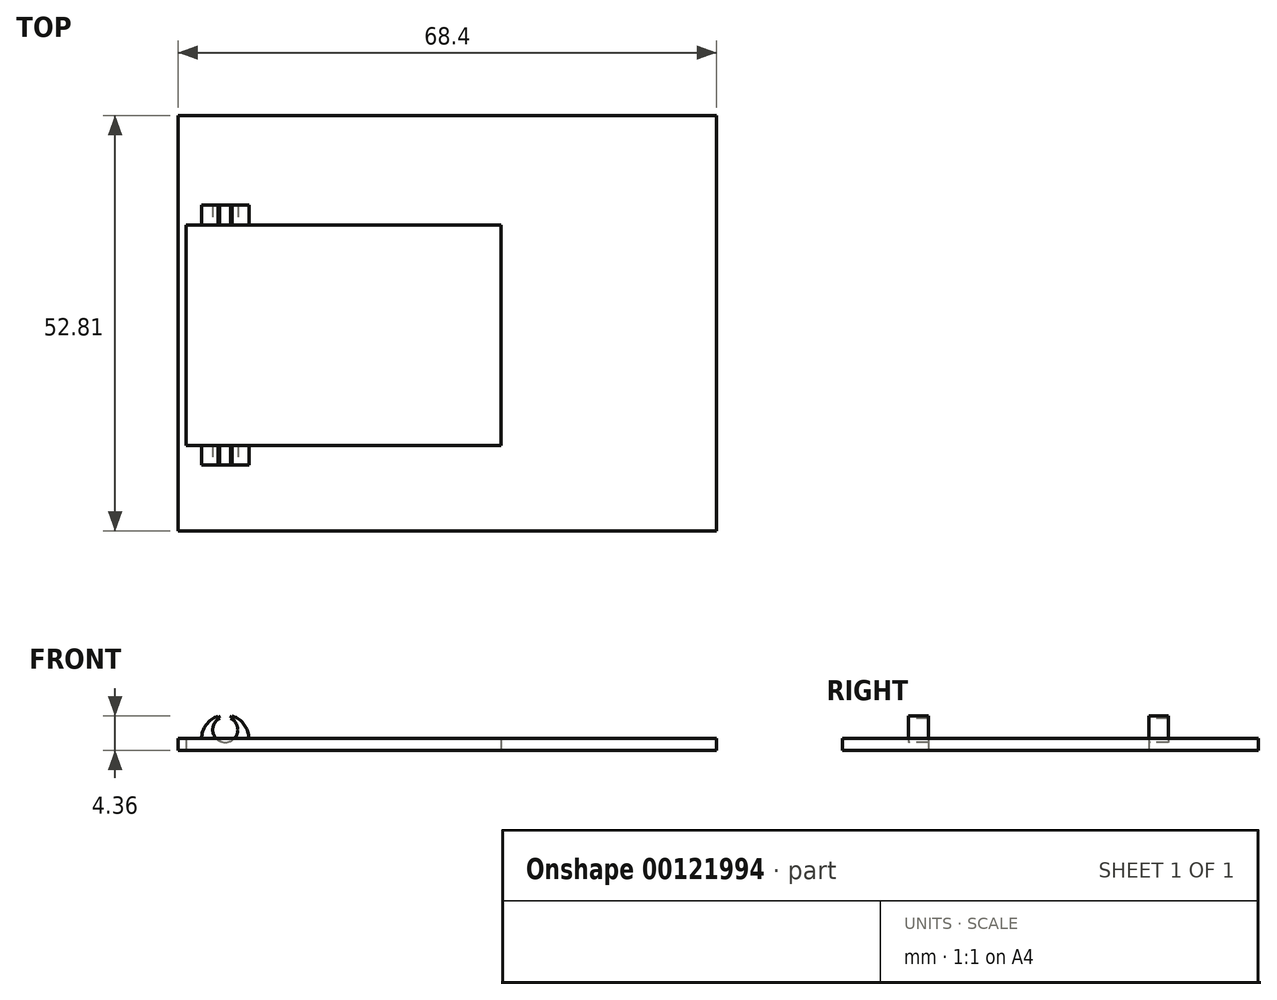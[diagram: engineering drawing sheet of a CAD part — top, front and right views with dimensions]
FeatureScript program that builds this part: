
annotation { "Feature Type Name" : "Feature", "Feature Type Description" : "" }
export const myFeature = defineFeature(function(context is Context, id is Id, definition is map)
    precondition{}
    {
        {
            var Q0;
            Q0=qCreatedBy(makeId("Front.planeOp"),FACE);
            var sketch = newSketch(context, id + "F0", { "sketchPlane" : qUnion([Q0])});
            skLineSegment(sketch, "E0.bottom", {"start": v(36.5, -11) * mm, "end": v(-36.5, -11) * mm});
            skLineSegment(sketch, "E0.top", {"start": v(36.5, 11) * mm, "end": v(-36.5, 11) * mm});
            skLineSegment(sketch, "E0.left", {"start": v(36.5, -11) * mm, "end": v(36.5, 11) * mm});
            skLineSegment(sketch, "E0.right", {"start": v(-36.5, -11) * mm, "end": v(-36.5, 11) * mm});
            skPoint(sketch, "E0.middle", {"position": v(0, 0) * mm});
            skFitSpline(sketch, "E1", {"points": [v(-0.93, -0.38) * mm, v(-0.75, 0.37) * mm], "startDerivative": vector(0.3, 0.98) * mm, "endDerivative": vector(-0.8, 0.77) * mm});
            skFitSpline(sketch, "E2", {"points": [v(0.91, -0.38) * mm, v(0.8, 0.37) * mm], "startDerivative": vector(-0.3, 0.98) * mm, "endDerivative": vector(1, 0.77) * mm});
            skSolve(sketch);
        }
        {
            var Q0;
            Q0=makeQuery(id+"F0.imprint","IMPRINT",FACE,{"disambiguationData":[TD([[makeQuery(id+"F0.imprint","IMPRINT",EDGE,{"derivedFrom":sQuery(id+"F0.wireOp",EDGE,"E0.bottom")}),-1.0]])]});
            extrude(context, id + "F1", {"entities" : qUnion([Q0]), "depth" : 58 * mm, "symmetric" : true});
        }
        {
            var Q0;
            Q0=makeQuery(id+"F1.opExtrude","SWEPT_FACE",FACE,{"disambiguationData":[OSD([sQuery(id+"F0.wireOp",EDGE,"E0.top")])]});
            var sketch = newSketch(context, id + "F2", { "sketchPlane" : qUnion([Q0])});
            skLineSegment(sketch, "E3.bottom", {"start": v(-34.5, 27) * mm, "end": v(34.5, 27) * mm});
            skLineSegment(sketch, "E3.top", {"start": v(-34.5, -27) * mm, "end": v(34.5, -27) * mm});
            skLineSegment(sketch, "E3.left", {"start": v(-34.5, 27) * mm, "end": v(-34.5, -27) * mm});
            skLineSegment(sketch, "E3.right", {"start": v(34.5, 27) * mm, "end": v(34.5, -27) * mm});
            skPoint(sketch, "E3.middle", {"position": v(0, 0) * mm});
            skSolve(sketch);
        }
        {
            var Q0;
            Q0=qSketchRegion(id+"F2",true);
            extrude(context, id + "F3", {"entities" : qUnion([Q0]), "operationType" : NewBodyOperationType.REMOVE, "oppositeDirection" : true, "depth" : 19 * mm});
        }
        {
            var Q0;
            Q0=makeQuery(id+"F1.opExtrude","SWEPT_FACE",FACE,{"disambiguationData":[OSD([sQuery(id+"F0.wireOp",EDGE,"E0.bottom")])]});
            var sketch = newSketch(context, id + "F4", { "sketchPlane" : qUnion([Q0])});
            skLineSegment(sketch, "E4.bottom", {"start": v(-33.5, 15) * mm, "end": v(8.5, 15) * mm});
            skLineSegment(sketch, "E4.top", {"start": v(-33.5, -13) * mm, "end": v(8.5, -13) * mm});
            skLineSegment(sketch, "E4.left", {"start": v(-33.5, 15) * mm, "end": v(-33.5, -13) * mm});
            skLineSegment(sketch, "E4.right", {"start": v(8.5, 15) * mm, "end": v(8.5, -13) * mm});
            skSolve(sketch);
        }
        {
            var Q0;
            Q0=qSketchRegion(id+"F4",true);
            extrude(context, id + "F5", {"entities" : qUnion([Q0]), "operationType" : NewBodyOperationType.REMOVE, "endBound" : BoundingType.THROUGH_ALL, "oppositeDirection" : true, "depth" : 25 * mm});
        }
        {
            var Q0;
            Q0=makeQuery(id+"F5.boolean.opBoolean","COPY",FACE,{"derivedFrom":makeQuery(id+"F5.opExtrude","SWEPT_FACE",FACE,{"disambiguationData":[OSD([sQuery(id+"F4.wireOp",EDGE,"E4.right")])]})});
            var sketch = newSketch(context, id + "F6", { "sketchPlane" : qUnion([Q0])});
            skLineSegment(sketch, "E5.bottom", {"start": v(-13, -8) * mm, "end": v(15, -8) * mm});
            skLineSegment(sketch, "E5.top", {"start": v(-13, -9.5) * mm, "end": v(15, -9.5) * mm});
            skLineSegment(sketch, "E5.left", {"start": v(-13, -8) * mm, "end": v(-13, -9.5) * mm});
            skLineSegment(sketch, "E5.right", {"start": v(15, -8) * mm, "end": v(15, -9.5) * mm});
            skSolve(sketch);
        }
        {
            var Q0;
            Q0=qSketchRegion(id+"F6",true);
            extrude(context, id + "F7", {"entities" : qUnion([Q0]), "operationType" : NewBodyOperationType.ADD, "depth" : 2 * mm});
        }
        {
            var Q0;
            Q0=makeQuery(id+"F1.opExtrude","CAP_FACE",FACE,{"disambiguationData":[OSD([sQuery(id+"F0.wireOp",EDGE,"E0.bottom"),sQuery(id+"F0.wireOp",EDGE,"E0.top"),sQuery(id+"F0.wireOp",EDGE,"E0.left"),sQuery(id+"F0.wireOp",EDGE,"E0.right")])],"isStart":false});
            var sketch = newSketch(context, id + "F8", { "sketchPlane" : qUnion([Q0])});
            skLineSegment(sketch, "E6.bottom", {"start": v(-36.5, 11) * mm, "end": v(36.5, 11) * mm});
            skLineSegment(sketch, "E6.top", {"start": v(-36.5, -2.74) * mm, "end": v(36.5, -2.74) * mm});
            skLineSegment(sketch, "E6.left", {"start": v(-36.5, 11) * mm, "end": v(-36.5, -2.74) * mm});
            skLineSegment(sketch, "E6.right", {"start": v(36.5, 11) * mm, "end": v(36.5, -2.74) * mm});
            skSolve(sketch);
        }
        {
            var Q0;
            Q0 = qSketchRegion(id + "F8", true);
            extrude(context, id + "F9", {"entities" : qUnion([Q0]), "operationType" : NewBodyOperationType.REMOVE, "endBound" : BoundingType.THROUGH_ALL, "oppositeDirection" : true, "depth" : 25 * mm});
        }
        {
            var Q0;
            Q0=makeQuery(id+"F7.boolean.opBoolean","MERGE",FACE,{"derivedFrom":[makeQuery(id+"F3.boolean.opBoolean","COPY",FACE,{"derivedFrom":makeQuery(id+"F3.opExtrude","CAP_FACE",FACE,{"disambiguationData":[OSD([sQuery(id+"F2.wireOp",EDGE,"E3.bottom"),sQuery(id+"F2.wireOp",EDGE,"E3.top"),sQuery(id+"F2.wireOp",EDGE,"E3.left"),sQuery(id+"F2.wireOp",EDGE,"E3.right")])],"isStart":false})}),makeQuery(id+"F7.opExtrude","SWEPT_FACE",FACE,{"disambiguationData":[OSD([sQuery(id+"F6.wireOp",EDGE,"E5.bottom")])]})]});
            var sketch = newSketch(context, id + "F10", { "sketchPlane" : qUnion([Q0])});
            skLineSegment(sketch, "E7.bottom", {"start": v(-31.5, 15.5) * mm, "end": v(-28.5, 15.5) * mm});
            skLineSegment(sketch, "E7.top", {"start": v(-31.5, 13) * mm, "end": v(-28.5, 13) * mm});
            skLineSegment(sketch, "E7.left", {"start": v(-31.5, 15.5) * mm, "end": v(-31.5, 13) * mm});
            skLineSegment(sketch, "E7.right", {"start": v(-28.5, 15.5) * mm, "end": v(-28.5, 13) * mm});
            skSolve(sketch);
        }
        {
            var Q0;
            Q0=makeQuery(id+"F10.imprint","IMPRINT",FACE,{"disambiguationData":[TD([[makeQuery(id+"F10.imprint","IMPRINT",EDGE,{"derivedFrom":sQuery(id+"F10.wireOp",EDGE,"E7.bottom")}),-1.0]])]});
            var Q1;
            Q1=sQuery(id+"F10.wireOp",EDGE,"E7.right");
            revolve(context, id + "F11", {"operationType" : NewBodyOperationType.ADD, "entities" : qUnion([Q0]), "axis" : qUnion([Q1]), "revolveType" : RevolveType.ONE_DIRECTION, "oppositeDirection" : true, "angle" : 180 * degree});
        }
        {
            var Q0;
            Q0=makeQuery(id+"F7.boolean.opBoolean","MERGE",FACE,{"derivedFrom":[makeQuery(id+"F3.boolean.opBoolean","COPY",FACE,{"derivedFrom":makeQuery(id+"F3.opExtrude","CAP_FACE",FACE,{"disambiguationData":[OSD([sQuery(id+"F2.wireOp",EDGE,"E3.bottom"),sQuery(id+"F2.wireOp",EDGE,"E3.top"),sQuery(id+"F2.wireOp",EDGE,"E3.left"),sQuery(id+"F2.wireOp",EDGE,"E3.right")])],"isStart":false})}),makeQuery(id+"F7.opExtrude","SWEPT_FACE",FACE,{"disambiguationData":[OSD([sQuery(id+"F6.wireOp",EDGE,"E5.bottom")])]})]});
            var sketch = newSketch(context, id + "F12", { "sketchPlane" : qUnion([Q0])});
            skLineSegment(sketch, "E8.bottom", {"start": v(-31.5, -15) * mm, "end": v(-28.5, -15) * mm});
            skLineSegment(sketch, "E8.top", {"start": v(-31.5, -17.5) * mm, "end": v(-28.5, -17.5) * mm});
            skLineSegment(sketch, "E8.left", {"start": v(-31.5, -15) * mm, "end": v(-31.5, -17.5) * mm});
            skLineSegment(sketch, "E8.right", {"start": v(-28.5, -15) * mm, "end": v(-28.5, -17.5) * mm});
            skSolve(sketch);
        }
        {
            var Q0;
            Q0=makeQuery(id+"F12.imprint","IMPRINT",FACE,{"disambiguationData":[TD([[makeQuery(id+"F12.imprint","IMPRINT",EDGE,{"derivedFrom":sQuery(id+"F12.wireOp",EDGE,"E8.bottom")}),1.0]])]});
            var Q1;
            Q1=sQuery(id+"F12.wireOp",EDGE,"E8.right");
            revolve(context, id + "F13", {"operationType" : NewBodyOperationType.ADD, "entities" : qUnion([Q0]), "axis" : qUnion([Q1]), "revolveType" : RevolveType.ONE_DIRECTION, "oppositeDirection" : true, "angle" : 180 * degree});
        }
        {
            var Q0;
            Q0=makeQuery(id+"F13.opRevolve","SWEPT_FACE",FACE,{"disambiguationData":[OSD([sQuery(id+"F12.wireOp",EDGE,"E8.top")])]});
            var sketch = newSketch(context, id + "F14", { "sketchPlane" : qUnion([Q0])});
            skCircle(sketch, "E9", {"center": v(-28.5, -6.87) * mm, "radius": 1.6 * mm});
            skPoint(sketch, "E9.centerSnap0", {"position": v(-28.5, -8) * mm});
            skSolve(sketch);
        }
        {
            var Q0;
            Q0 = qSketchRegion(id + "F14", true);
            extrude(context, id + "F15", {"entities" : qUnion([Q0]), "operationType" : NewBodyOperationType.REMOVE, "oppositeDirection" : true, "depth" : 33 * mm});
        }
        {
            var Q0;
            Q0=makeQuery(id+"F1.opExtrude","CAP_FACE",FACE,{"disambiguationData":[OSD([sQuery(id+"F0.wireOp",EDGE,"E0.bottom"),sQuery(id+"F0.wireOp",EDGE,"E0.top"),sQuery(id+"F0.wireOp",EDGE,"E0.left"),sQuery(id+"F0.wireOp",EDGE,"E0.right")])],"isStart":true});
            var sketch = newSketch(context, id + "F16", { "sketchPlane" : qUnion([Q0])});
            skLineSegment(sketch, "E10.bottom", {"start": v(-36.5, -2.74) * mm, "end": v(36.5, -2.74) * mm});
            skLineSegment(sketch, "E10.top", {"start": v(-36.5, -11) * mm, "end": v(36.5, -11) * mm});
            skLineSegment(sketch, "E10.left", {"start": v(-36.5, -2.74) * mm, "end": v(-36.5, -11) * mm});
            skLineSegment(sketch, "E10.right", {"start": v(36.5, -2.74) * mm, "end": v(36.5, -11) * mm});
            skSolve(sketch);
        }
        {
            var Q0;
            Q0 = qSketchRegion(id + "F16", true);
            extrude(context, id + "F17", {"entities" : qUnion([Q0]), "operationType" : NewBodyOperationType.REMOVE, "oppositeDirection" : true, "depth" : 2.09 * mm});
        }
        {
            var Q0;
            Q0=makeQuery(id+"F1.opExtrude","SWEPT_FACE",FACE,{"disambiguationData":[OSD([sQuery(id+"F0.wireOp",EDGE,"E0.left")])]});
            var sketch = newSketch(context, id + "F18", { "sketchPlane" : qUnion([Q0])});
            skLineSegment(sketch, "E11.bottom", {"start": v(-29, -2.74) * mm, "end": v(26.91, -2.74) * mm});
            skLineSegment(sketch, "E11.top", {"start": v(-29, -11) * mm, "end": v(26.91, -11) * mm});
            skLineSegment(sketch, "E11.left", {"start": v(-29, -2.74) * mm, "end": v(-29, -11) * mm});
            skLineSegment(sketch, "E11.right", {"start": v(26.91, -2.74) * mm, "end": v(26.91, -11) * mm});
            skSolve(sketch);
        }
        {
            var Q0;
            Q0 = qSketchRegion(id + "F18", true);
            extrude(context, id + "F19", {"entities" : qUnion([Q0]), "operationType" : NewBodyOperationType.REMOVE, "oppositeDirection" : true, "depth" : 2.6 * mm});
        }
        {
            var Q0;
            Q0=makeQuery(id+"F1.opExtrude","CAP_FACE",FACE,{"disambiguationData":[OSD([sQuery(id+"F0.wireOp",EDGE,"E0.bottom"),sQuery(id+"F0.wireOp",EDGE,"E0.top"),sQuery(id+"F0.wireOp",EDGE,"E0.left"),sQuery(id+"F0.wireOp",EDGE,"E0.right")])],"isStart":false});
            var sketch = newSketch(context, id + "F20", { "sketchPlane" : qUnion([Q0])});
            skLineSegment(sketch, "E12.bottom", {"start": v(-36.5, -2.74) * mm, "end": v(33.9, -2.74) * mm});
            skLineSegment(sketch, "E12.top", {"start": v(-36.5, -11) * mm, "end": v(33.9, -11) * mm});
            skLineSegment(sketch, "E12.left", {"start": v(-36.5, -2.74) * mm, "end": v(-36.5, -11) * mm});
            skLineSegment(sketch, "E12.right", {"start": v(33.9, -2.74) * mm, "end": v(33.9, -11) * mm});
            skSolve(sketch);
        }
        {
            var Q0;
            Q0 = qSketchRegion(id + "F20", true);
            extrude(context, id + "F21", {"entities" : qUnion([Q0]), "operationType" : NewBodyOperationType.REMOVE, "oppositeDirection" : true, "depth" : 3.1 * mm});
        }
        {
            var Q0;
            Q0=makeQuery(id+"F1.opExtrude","SWEPT_FACE",FACE,{"disambiguationData":[OSD([sQuery(id+"F0.wireOp",EDGE,"E0.right")])]});
            var sketch = newSketch(context, id + "F22", { "sketchPlane" : qUnion([Q0])});
            skLineSegment(sketch, "E13.bottom", {"start": v(-26.91, -2.74) * mm, "end": v(25.9, -2.74) * mm});
            skLineSegment(sketch, "E13.top", {"start": v(-26.91, -11) * mm, "end": v(25.9, -11) * mm});
            skLineSegment(sketch, "E13.left", {"start": v(-26.91, -2.74) * mm, "end": v(-26.91, -11) * mm});
            skLineSegment(sketch, "E13.right", {"start": v(25.9, -2.74) * mm, "end": v(25.9, -11) * mm});
            skSolve(sketch);
        }
        {
            var Q0;
            Q0 = qSketchRegion(id + "F22", true);
            extrude(context, id + "F23", {"entities" : qUnion([Q0]), "operationType" : NewBodyOperationType.REMOVE, "oppositeDirection" : true, "depth" : 2 * mm});
        }
        {
            var Q0;
            Q0=makeQuery(id+"F17.boolean.opBoolean","COPY",FACE,{"derivedFrom":makeQuery(id+"F17.opExtrude","CAP_FACE",FACE,{"disambiguationData":[OSD([sQuery(id+"F16.wireOp",EDGE,"E10.bottom"),sQuery(id+"F16.wireOp",EDGE,"E10.top"),sQuery(id+"F16.wireOp",EDGE,"E10.left"),sQuery(id+"F16.wireOp",EDGE,"E10.right")])],"isStart":false})});
            var sketch = newSketch(context, id + "F24", { "sketchPlane" : qUnion([Q0])});
            skLineSegment(sketch, "E14.bottom", {"start": v(-33.9, -11) * mm, "end": v(34.5, -11) * mm});
            skLineSegment(sketch, "E14.top", {"start": v(-33.9, -9.5) * mm, "end": v(34.5, -9.5) * mm});
            skLineSegment(sketch, "E14.left", {"start": v(-33.9, -11) * mm, "end": v(-33.9, -9.5) * mm});
            skLineSegment(sketch, "E14.right", {"start": v(34.5, -11) * mm, "end": v(34.5, -9.5) * mm});
            skSolve(sketch);
        }
        {
            var Q0;
            Q0 = qSketchRegion(id + "F24", true);
            extrude(context, id + "F25", {"entities" : qUnion([Q0]), "operationType" : NewBodyOperationType.REMOVE, "endBound" : BoundingType.THROUGH_ALL, "oppositeDirection" : true, "depth" : 25 * mm});
        }
        {
            var Q0;
            Q0=makeQuery(id+"F13.opRevolve","SWEPT_FACE",FACE,{"disambiguationData":[OSD([sQuery(id+"F12.wireOp",EDGE,"E8.top")])]});
            var sketch = newSketch(context, id + "F26", { "sketchPlane" : qUnion([Q0])});
            skLineSegment(sketch, "E15", {"start": v(-29.4, -5.14) * mm, "end": v(-29.2, -5.43) * mm});
            skLineSegment(sketch, "E16", {"start": v(-29.2, -5.43) * mm, "end": v(-27.8, -5.43) * mm});
            skLineSegment(sketch, "E17", {"start": v(-27.8, -5.43) * mm, "end": v(-27.6, -5.14) * mm});
            skSolve(sketch);
        }
        {
            var Q0;
            Q0 = qSketchRegion(id + "F26", true);
            var Q1;
            {var subQ0=sQuery(id+"F26.wireOp",EDGE,"E15");Q1=makeQuery(id+"F26.imprint","IMPRINT",FACE,{"disambiguationData":[TD([[makeQuery(id+"F26.imprint","IMPRINT",EDGE,{"derivedFrom":subQ0}),1.0]])]});}
            extrude(context, id + "F27", {"entities" : qUnion([Q0, Q1]), "operationType" : NewBodyOperationType.REMOVE, "oppositeDirection" : true, "depth" : 35.4 * mm});
        }
    });
